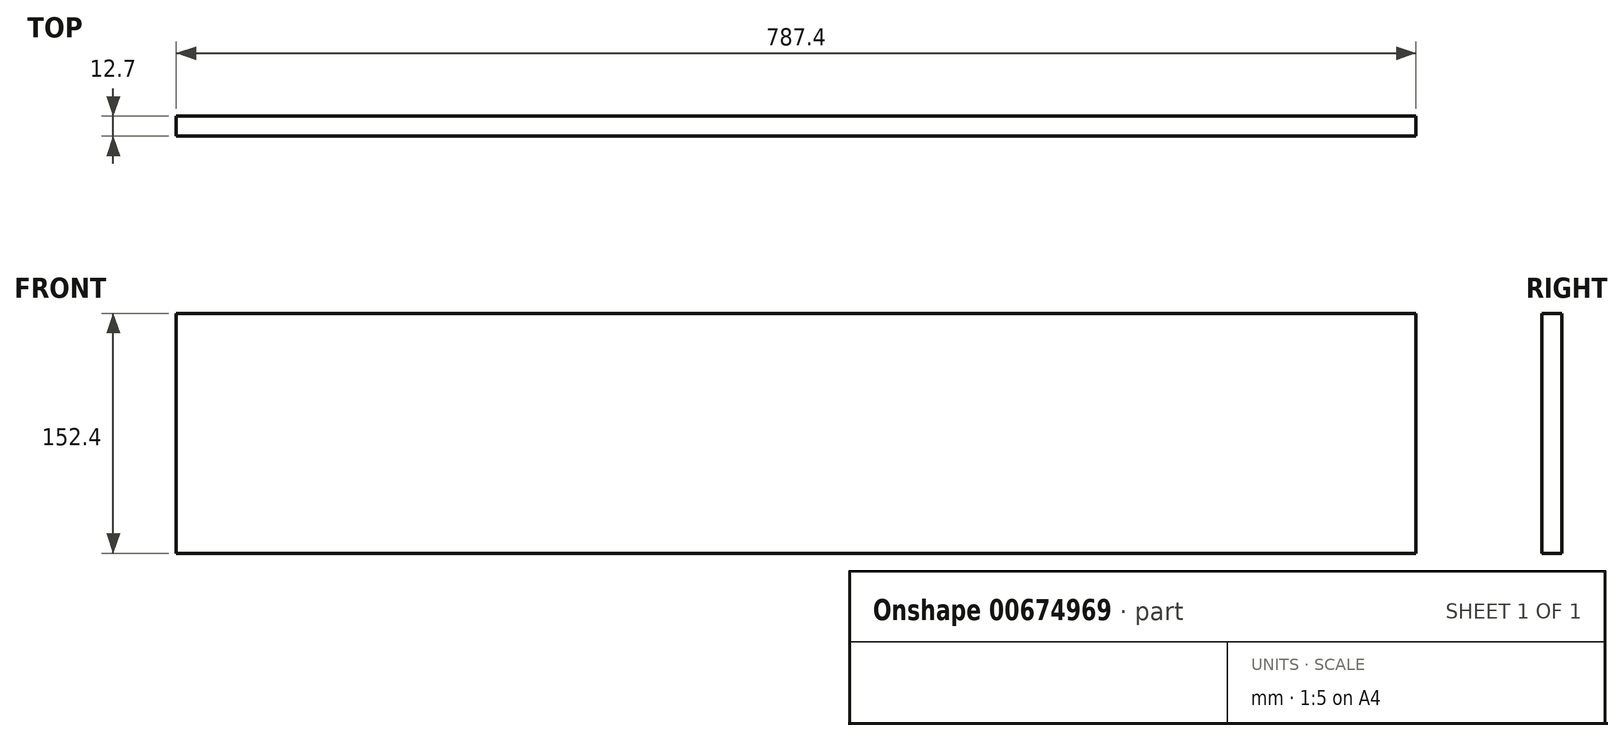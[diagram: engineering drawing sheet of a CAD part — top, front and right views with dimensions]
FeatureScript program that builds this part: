
annotation { "Feature Type Name" : "Feature", "Feature Type Description" : "" }
export const myFeature = defineFeature(function(context is Context, id is Id, definition is map)
    precondition{}
    {
        {
            var Q0;
            Q0=qCreatedBy(makeId("Front.planeOp"),FACE);
            var sketch = newSketch(context, id + "F0", { "sketchPlane" : qUnion([Q0])});
            skLineSegment(sketch, "E0.bottom", {"start": v(0, 0) * mm, "end": v(787.4, 0) * mm});
            skLineSegment(sketch, "E0.top", {"start": v(0, 152.4) * mm, "end": v(787.4, 152.4) * mm});
            skLineSegment(sketch, "E0.left", {"start": v(0, 0) * mm, "end": v(0, 152.4) * mm});
            skLineSegment(sketch, "E0.right", {"start": v(787.4, 0) * mm, "end": v(787.4, 152.4) * mm});
            skSolve(sketch);
        }
        {
            var Q0;
            Q0 = qSketchRegion(id + "F0", true);
            extrude(context, id + "F1", {"entities" : qUnion([Q0]), "depth" : 12.7 * mm, "offsetDistance" : 25.4 * mm});
        }
    });
